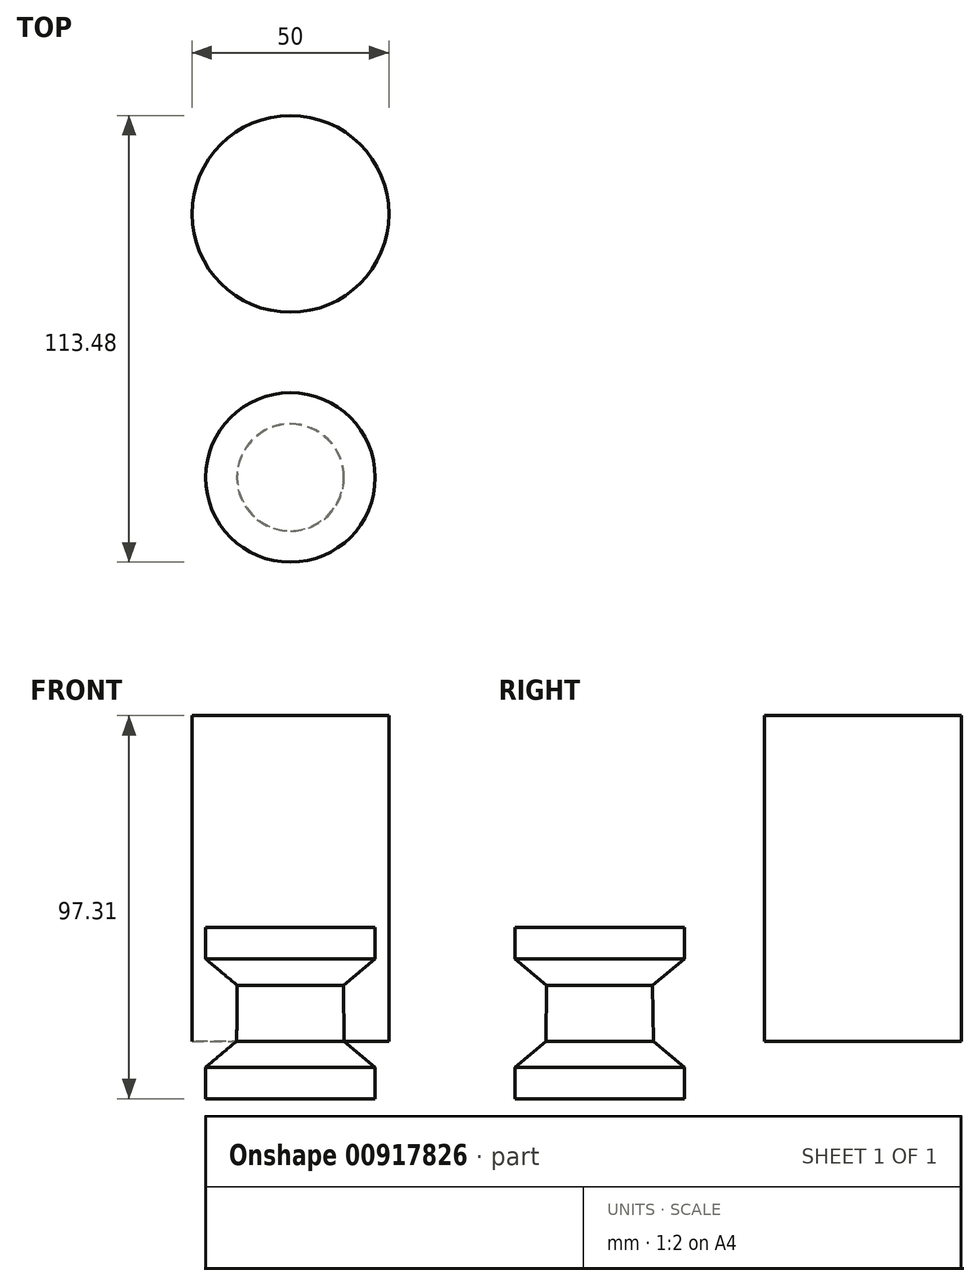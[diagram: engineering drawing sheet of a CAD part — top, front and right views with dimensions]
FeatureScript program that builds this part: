
annotation { "Feature Type Name" : "Feature", "Feature Type Description" : "" }
export const myFeature = defineFeature(function(context is Context, id is Id, definition is map)
    precondition{}
    {
        {
            var Q0;
            Q0=qCreatedBy(makeId("Top.planeOp"),FACE);
            var sketch = newSketch(context, id + "F0", { "sketchPlane" : qUnion([Q0])});
            skCircle(sketch, "E0", {"center": v(0, 0) * mm, "radius": 25 * mm});
            skSolve(sketch);
        }
        {
            var Q0;
            Q0=makeQuery(id+"F0.imprint","IMPRINT",FACE,{"disambiguationData":[TD([[makeQuery(id+"F0.imprint","IMPRINT",EDGE,{"derivedFrom":sQuery(id+"F0.wireOp",EDGE,"E0")}),1.0]])]});
            extrude(context, id + "F1", {"entities" : qUnion([Q0]), "depth" : 82.7 * mm, "offsetDistance" : 25 * mm});
        }
        {
            var Q0;
            Q0=qCreatedBy(makeId("Right.planeOp"),FACE);
            var sketch = newSketch(context, id + "F2", { "sketchPlane" : qUnion([Q0])});
            skLineSegment(sketch, "E1.bottom", {"start": v(-66.95, -14.61) * mm, "end": v(-88.48, -14.61) * mm});
            skLineSegment(sketch, "E1.top", {"start": v(-66.95, 28.9) * mm, "end": v(-88.48, 28.9) * mm});
            skLineSegment(sketch, "E1.left", {"start": v(-66.95, -14.61) * mm, "end": v(-66.95, 28.9) * mm});
            skPoint(sketch, "E1.middle", {"position": v(-77.72, 7.14) * mm});
            skLineSegment(sketch, "E2", {"start": v(-88.48, 28.9) * mm, "end": v(-88.48, 20.9) * mm});
            skLineSegment(sketch, "E3", {"start": v(-88.48, -14.61) * mm, "end": v(-88.48, -6.61) * mm});
            skLineSegment(sketch, "E4", {"start": v(-88.48, -6.61) * mm, "end": v(-80.6, 0) * mm});
            skLineSegment(sketch, "E5", {"start": v(-88.48, 20.9) * mm, "end": v(-80.46, 14.17) * mm});
            skLineSegment(sketch, "E6", {"start": v(-80.46, 14.17) * mm, "end": v(-80.6, 0) * mm});
            skSolve(sketch);
        }
        {
            var Q0;
            Q0=makeQuery(id+"F2.imprint","IMPRINT",FACE,{"disambiguationData":[TD([[makeQuery(id+"F2.imprint","IMPRINT",EDGE,{"derivedFrom":sQuery(id+"F2.wireOp",EDGE,"E1.bottom")}),-1.0]])]});
            var Q1;
            Q1=sQuery(id+"F2.wireOp",EDGE,"E1.left");
            revolve(context, id + "F3", {"surfaceOperationType" : NewSurfaceOperationType.NEW, "entities" : qUnion([Q0]), "axis" : qUnion([Q1]), "revolveType" : RevolveType.FULL});
        }
    });
